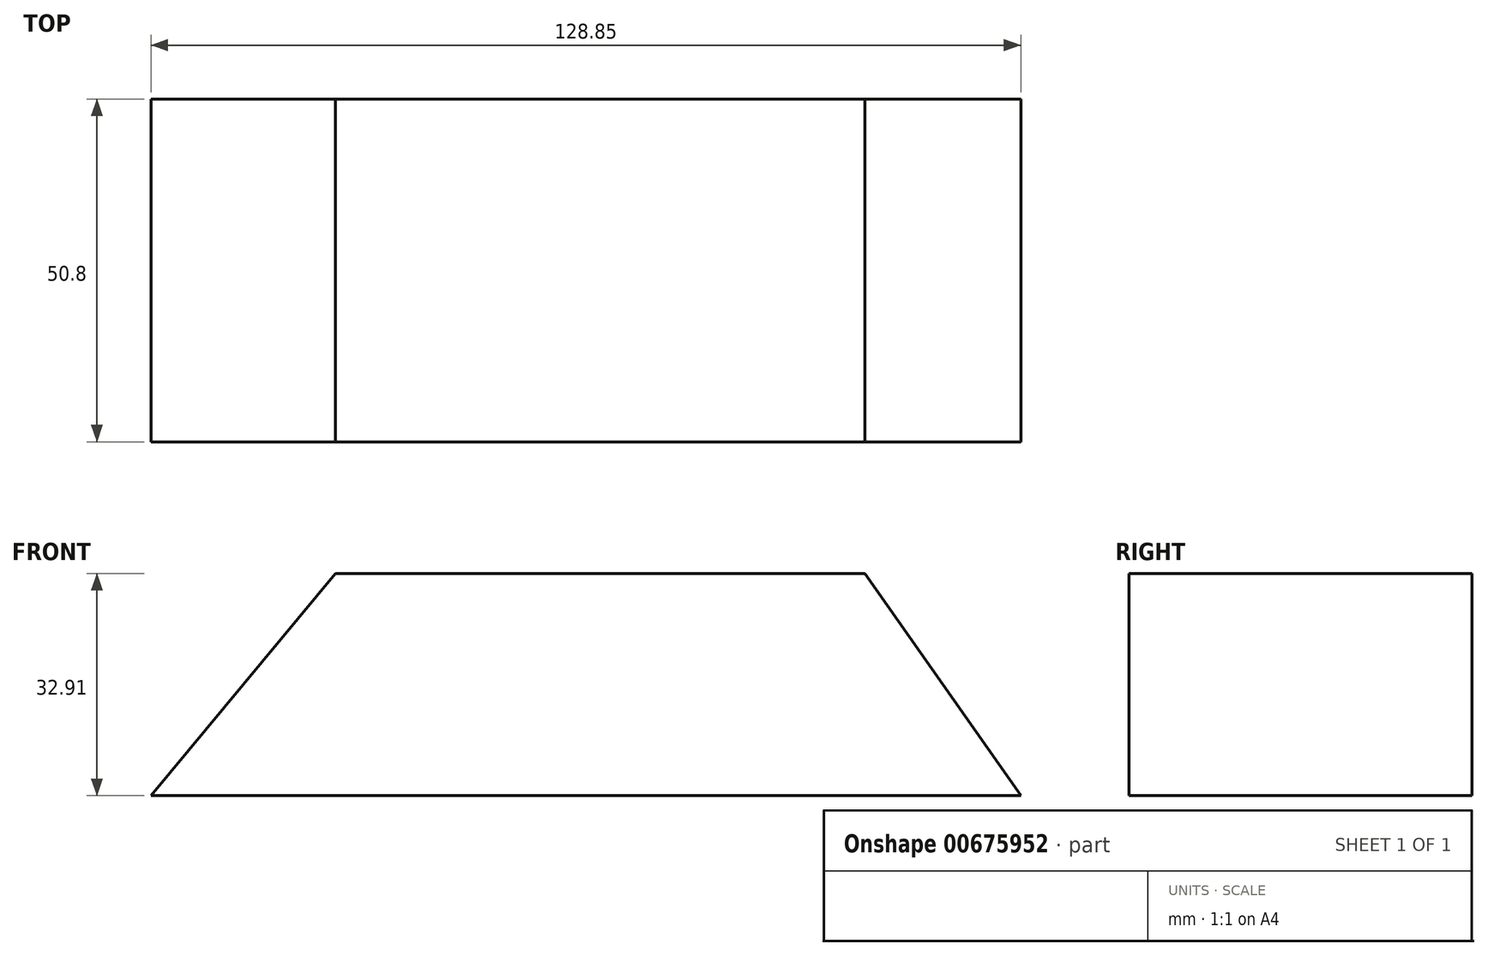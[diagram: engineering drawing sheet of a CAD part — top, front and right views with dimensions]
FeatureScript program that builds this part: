
annotation { "Feature Type Name" : "Feature", "Feature Type Description" : "" }
export const myFeature = defineFeature(function(context is Context, id is Id, definition is map)
    precondition{}
    {
        {
            var Q0;
            Q0=qCreatedBy(makeId("Front.planeOp"),FACE);
            var sketch = newSketch(context, id + "F0", { "sketchPlane" : qUnion([Q0])});
            skLineSegment(sketch, "E0", {"start": v(-64.25, -32.91) * mm, "end": v(64.6, -32.91) * mm});
            skLineSegment(sketch, "E1", {"start": v(64.6, -32.91) * mm, "end": v(41.5, 0) * mm});
            skLineSegment(sketch, "E2", {"start": v(41.5, 0) * mm, "end": v(-36.94, 0) * mm});
            skLineSegment(sketch, "E3", {"start": v(-64.25, -32.91) * mm, "end": v(-36.94, 0) * mm});
            skSolve(sketch);
        }
        {
            var Q0;
            Q0=makeQuery(id+"F0.imprint","IMPRINT",FACE,{"disambiguationData":[TD([[makeQuery(id+"F0.imprint","IMPRINT",EDGE,{"derivedFrom":sQuery(id+"F0.wireOp",EDGE,"E0")}),1.0]])]});
            extrude(context, id + "F1", {"entities" : qUnion([Q0]), "depth" : 50.8 * mm, "offsetDistance" : 25.4 * mm});
        }
    });
